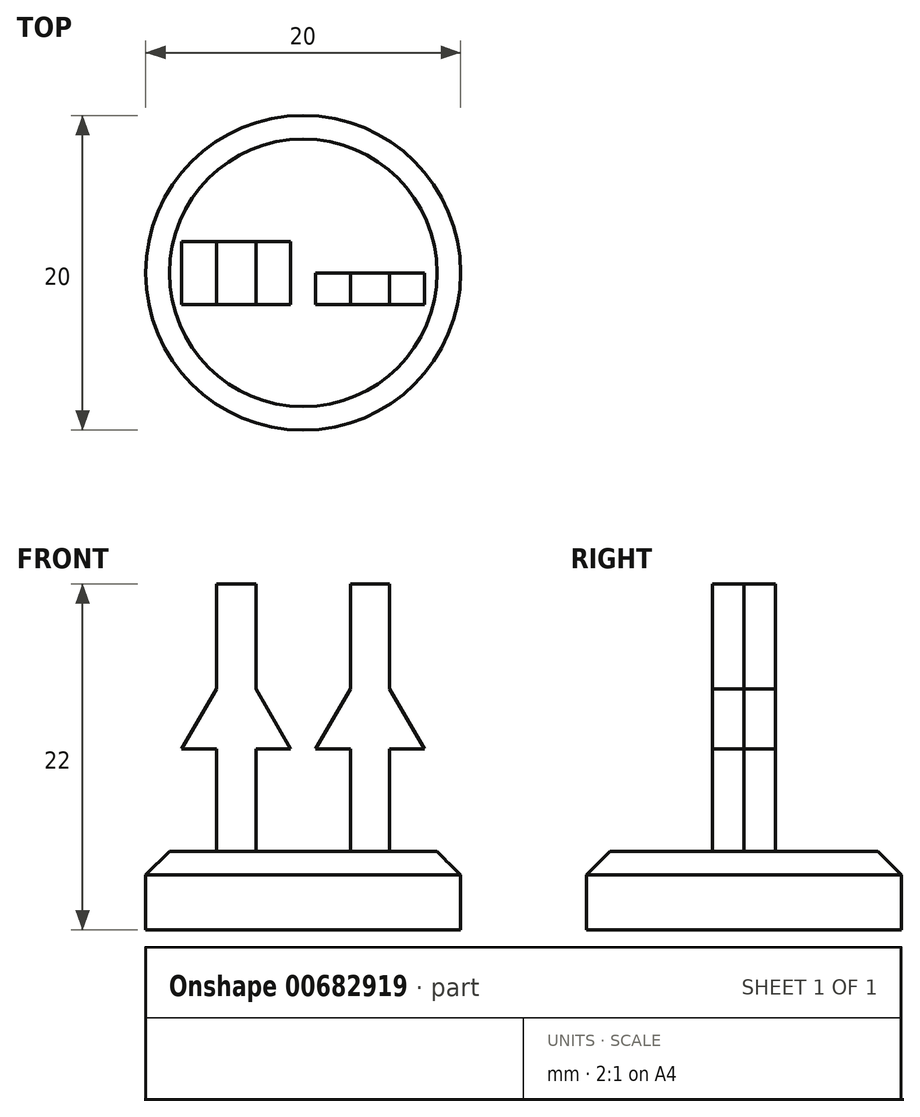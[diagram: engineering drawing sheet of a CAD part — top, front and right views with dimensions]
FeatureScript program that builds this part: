
annotation { "Feature Type Name" : "Feature", "Feature Type Description" : "" }
export const myFeature = defineFeature(function(context is Context, id is Id, definition is map)
    precondition{}
    {
        {
            var Q0;
            Q0=qCreatedBy(makeId("Top.planeOp"),FACE);
            var sketch = newSketch(context, id + "F0", { "sketchPlane" : qUnion([Q0])});
            skCircle(sketch, "E0", {"center": v(0, 0) * mm, "radius": 10 * mm});
            skSolve(sketch);
        }
        {
            var Q0;
            Q0=makeQuery(id+"F0.imprint","IMPRINT",FACE,{"disambiguationData":[TD([[makeQuery(id+"F0.imprint","IMPRINT",EDGE,{"derivedFrom":sQuery(id+"F0.wireOp",EDGE,"E0")}),1.0]])]});
            extrude(context, id + "F1", {"entities" : qUnion([Q0]), "depth" : 5 * mm, "offsetDistance" : 25 * mm});
        }
        {
            var Q0;
            Q0=makeQuery(id+"F1.opExtrude","CAP_EDGE",EDGE,{"disambiguationData":[OSD([sQuery(id+"F0.wireOp",EDGE,"E0")])],"isStart":false});
            chamfer(context, id + "F2", {"entities" : qUnion([Q0]), "width" : 1.5 * mm, "tangentPropagation" : true});
        }
        {
            var Q0;
            Q0=qCreatedBy(makeId("Front.planeOp"),FACE);
            var sketch = newSketch(context, id + "F3", { "sketchPlane" : qUnion([Q0])});
            skLineSegment(sketch, "E1", {"start": v(5.5, 13.5) * mm, "end": v(5.5, 5) * mm});
            skLineSegment(sketch, "E2", {"start": v(5.5, 13.5) * mm, "end": v(5.5, 22) * mm});
            skLineSegment(sketch, "E3", {"start": v(5.5, 22) * mm, "end": v(3, 22) * mm});
            skLineSegment(sketch, "E4", {"start": v(3, 22) * mm, "end": v(3, 5) * mm});
            skLineSegment(sketch, "E5", {"start": v(3, 5) * mm, "end": v(5.5, 5) * mm});
            skLineSegment(sketch, "E6", {"start": v(5.5, 13.5) * mm, "end": v(3, 13.5) * mm});
            skCircle(sketch, "E7.cCircle", {"center": v(4.25, 13.5) * mm, "radius": 2 * mm, "construction": true});
            skLineSegment(sketch, "E7.0", {"start": v(0.79, 11.5) * mm, "end": v(4.25, 17.5) * mm});
            skLineSegment(sketch, "E7.1", {"start": v(4.25, 17.5) * mm, "end": v(7.71, 11.5) * mm});
            skLineSegment(sketch, "E7.2", {"start": v(7.71, 11.5) * mm, "end": v(0.79, 11.5) * mm});
            skPoint(sketch, "E7.0.midPoint", {"position": v(2.52, 14.5) * mm});
            skLineSegment(sketch, "E8", {"start": v(5.5, 13.5) * mm, "end": v(5.5, 8.5) * mm});
            skLineSegment(sketch, "E9", {"start": v(5.5, 8.5) * mm, "end": v(5.5, 8) * mm});
            skLineSegment(sketch, "E10", {"start": v(5.5, 8.5) * mm, "end": v(5.5, 9) * mm});
            skLineSegment(sketch, "E11", {"start": v(-5.5, 9) * mm, "end": v(-5.5, 8) * mm});
            skLineSegment(sketch, "E12", {"start": v(5.5, 13.5) * mm, "end": v(5.5, 18.5) * mm});
            skLineSegment(sketch, "E13", {"start": v(5.5, 18.5) * mm, "end": v(5.5, 19) * mm});
            skLineSegment(sketch, "E14", {"start": v(-3.5, 19) * mm, "end": v(-3.5, 18) * mm});
            skLineSegment(sketch, "E15", {"start": v(-5.5, 8) * mm, "end": v(-5.5, 5) * mm});
            skLineSegment(sketch, "E16", {"start": v(-5.5, 5) * mm, "end": v(-3, 5) * mm});
            skLineSegment(sketch, "E17", {"start": v(-3, 5) * mm, "end": v(-3, 22) * mm});
            skLineSegment(sketch, "E18", {"start": v(-3, 22) * mm, "end": v(-5.5, 22) * mm});
            skLineSegment(sketch, "E19", {"start": v(-5.5, 22) * mm, "end": v(-5.5, 9) * mm});
            skLineSegment(sketch, "E20", {"start": v(-3, 13.5) * mm, "end": v(-5.5, 13.5) * mm});
            skCircle(sketch, "E21.cCircle", {"center": v(-4.25, 13.5) * mm, "radius": 2 * mm, "construction": true});
            skLineSegment(sketch, "E21.0", {"start": v(-7.71, 11.5) * mm, "end": v(-4.25, 17.5) * mm});
            skLineSegment(sketch, "E21.1", {"start": v(-4.25, 17.5) * mm, "end": v(-0.79, 11.5) * mm});
            skLineSegment(sketch, "E21.2", {"start": v(-0.79, 11.5) * mm, "end": v(-7.71, 11.5) * mm});
            skPoint(sketch, "E21.0.midPoint", {"position": v(-5.98, 14.5) * mm});
            skSolve(sketch);
        }
        {
            var Q0;
            {var subQ0=sQuery(id+"F3.wireOp",EDGE,"E15");Q0=makeQuery(id+"F3.imprint","IMPRINT",FACE,{"disambiguationData":[TD([[makeQuery(id+"F3.imprint","IMPRINT",EDGE,{"derivedFrom":subQ0}),1.0]])]});}
            var Q1;
            {var subQ0=sQuery(id+"F3.wireOp",EDGE,"E11");Q1=makeQuery(id+"F3.imprint","IMPRINT",FACE,{"disambiguationData":[TD([[makeQuery(id+"F3.imprint","IMPRINT",EDGE,{"derivedFrom":subQ0}),1.0]])]});}
            var Q2;
            {var subQ1=sQuery(id+"F3.wireOp",EDGE,"EQHTsxDi-yBak-7mSX-J8Yb-3IxzzojTnzbz");var subQ3=sQuery(id+"F3.wireOp",EDGE,"E17");var subQ4=makeQuery(id+"F3.imprint","INTERSECT",VERTEX,{"derivedFrom":[subQ1,subQ3]});Q2=makeQuery(id+"F3.imprint","IMPRINT",FACE,{"disambiguationData":[TD([[makeQuery(id+"F3.imprint","IMPRINT",EDGE,{"disambiguationData":[TD([[subQ4,-1.0]])],"derivedFrom":subQ3}),1.0]])]});}
            var Q3;
            {var subQ0=sQuery(id+"F3.wireOp",EDGE,"E17");var subQ1=makeQuery(id+"F3.imprint","INTERSECT",VERTEX,{"derivedFrom":[subQ0,sQuery(id+"F3.wireOp",EDGE,"E20")]});Q3=makeQuery(id+"F3.imprint","IMPRINT",FACE,{"disambiguationData":[TD([[makeQuery(id+"F3.imprint","IMPRINT",EDGE,{"disambiguationData":[TD([[subQ1,1.0]])],"derivedFrom":subQ0}),-1.0]])]});}
            var Q4;
            {var subQ0=sQuery(id+"F3.wireOp",EDGE,"E20");Q4=makeQuery(id+"F3.imprint","IMPRINT",FACE,{"disambiguationData":[TD([[makeQuery(id+"F3.imprint","IMPRINT",EDGE,{"derivedFrom":subQ0}),1.0]])]});}
            var Q5;
            {var subQ0=sQuery(id+"F3.wireOp",EDGE,"E20");Q5=makeQuery(id+"F3.imprint","IMPRINT",FACE,{"disambiguationData":[TD([[makeQuery(id+"F3.imprint","IMPRINT",EDGE,{"derivedFrom":subQ0}),-1.0]])]});}
            var Q6;
            {var subQ0=sQuery(id+"F3.wireOp",EDGE,"E19");var subQ1=makeQuery(id+"F3.imprint","INTERSECT",VERTEX,{"derivedFrom":[subQ0,sQuery(id+"F3.wireOp",EDGE,"E20")]});Q6=makeQuery(id+"F3.imprint","IMPRINT",FACE,{"disambiguationData":[TD([[makeQuery(id+"F3.imprint","IMPRINT",EDGE,{"disambiguationData":[TD([[subQ1,1.0]])],"derivedFrom":subQ0}),-1.0]])]});}
            var Q7;
            {var subQ3=sQuery(id+"F3.wireOp",EDGE,"E19");var subQ5=sQuery(id+"F3.wireOp",EDGE,"8I4BeRHs-Gmml-n6d2-LC97-bdPFLSqAeQXX");var subQ6=makeQuery(id+"F3.imprint","INTERSECT",VERTEX,{"derivedFrom":[subQ5,subQ3]});Q7=makeQuery(id+"F3.imprint","IMPRINT",FACE,{"disambiguationData":[TD([[makeQuery(id+"F3.imprint","IMPRINT",EDGE,{"disambiguationData":[TD([[subQ6,-1.0]])],"derivedFrom":subQ5}),-1.0]])]});}
            var Q8;
            {var subQ0=sQuery(id+"F3.wireOp",EDGE,"E19");var subQ1=sQuery(id+"F3.wireOp",EDGE,"mUdp0F8c-JpfW-iBtl-aqys-KmnHf74pH5AF");var subQ2=makeQuery(id+"F3.imprint","INTERSECT",VERTEX,{"derivedFrom":[subQ1,subQ0]});Q8=makeQuery(id+"F3.imprint","IMPRINT",FACE,{"disambiguationData":[TD([[makeQuery(id+"F3.imprint","IMPRINT",EDGE,{"disambiguationData":[TD([[subQ2,1.0]])],"derivedFrom":subQ1}),1.0]])]});}
            var Q9;
            {var subQ5=sQuery(id+"F3.wireOp",EDGE,"E18");Q9=makeQuery(id+"F3.imprint","IMPRINT",FACE,{"disambiguationData":[TD([[makeQuery(id+"F3.imprint","IMPRINT",EDGE,{"derivedFrom":subQ5}),1.0]])]});}
            var Q10;
            {var subQ0=sQuery(id+"F3.wireOp",EDGE,"E2");Q10=makeQuery(id+"F3.imprint","IMPRINT",FACE,{"disambiguationData":[TD([[makeQuery(id+"F3.imprint","IMPRINT",EDGE,{"derivedFrom":subQ0}),1.0]])]});}
            var Q11;
            {var subQ1=sQuery(id+"F3.wireOp",EDGE,"E13");Q11=makeQuery(id+"F3.imprint","IMPRINT",FACE,{"disambiguationData":[TD([[makeQuery(id+"F3.imprint","IMPRINT",EDGE,{"derivedFrom":subQ1}),1.0]])]});}
            var Q12;
            {var subQ0=sQuery(id+"F3.wireOp",EDGE,"mUdp0F8c-JpfW-iBtl-aqys-KmnHf74pH5AF");var subQ1=sQuery(id+"F3.wireOp",EDGE,"E4");var subQ2=makeQuery(id+"F3.imprint","INTERSECT",VERTEX,{"derivedFrom":[subQ1,subQ0]});Q12=makeQuery(id+"F3.imprint","IMPRINT",FACE,{"disambiguationData":[TD([[makeQuery(id+"F3.imprint","IMPRINT",EDGE,{"disambiguationData":[TD([[subQ2,-1.0]])],"derivedFrom":subQ1}),-1.0]])]});}
            var Q13;
            {var subQ0=sQuery(id+"F3.wireOp",EDGE,"8I4BeRHs-Gmml-n6d2-LC97-bdPFLSqAeQXX");var subQ7=sQuery(id+"F3.wireOp",EDGE,"E4");var subQ9=makeQuery(id+"F3.imprint","INTERSECT",VERTEX,{"derivedFrom":[subQ7,subQ0]});Q13=makeQuery(id+"F3.imprint","IMPRINT",FACE,{"disambiguationData":[TD([[makeQuery(id+"F3.imprint","IMPRINT",EDGE,{"disambiguationData":[TD([[subQ9,-1.0]])],"derivedFrom":subQ7}),1.0]])]});}
            var Q14;
            {var subQ7=sQuery(id+"F3.wireOp",EDGE,"E6");Q14=makeQuery(id+"F3.imprint","IMPRINT",FACE,{"disambiguationData":[TD([[makeQuery(id+"F3.imprint","IMPRINT",EDGE,{"derivedFrom":subQ7}),-1.0]])]});}
            var Q15;
            {var subQ0=sQuery(id+"F3.wireOp",EDGE,"E4");var subQ1=makeQuery(id+"F3.imprint","INTERSECT",VERTEX,{"derivedFrom":[subQ0,sQuery(id+"F3.wireOp",EDGE,"E6")]});Q15=makeQuery(id+"F3.imprint","IMPRINT",FACE,{"disambiguationData":[TD([[makeQuery(id+"F3.imprint","IMPRINT",EDGE,{"disambiguationData":[TD([[subQ1,1.0]])],"derivedFrom":subQ0}),-1.0]])]});}
            var Q16;
            {var subQ0=sQuery(id+"F3.wireOp",EDGE,"E6");Q16=makeQuery(id+"F3.imprint","IMPRINT",FACE,{"disambiguationData":[TD([[makeQuery(id+"F3.imprint","IMPRINT",EDGE,{"derivedFrom":subQ0}),1.0]])]});}
            var Q17;
            {var subQ3=sQuery(id+"F3.wireOp",EDGE,"E7.1");var subQ5=sQuery(id+"F3.wireOp",EDGE,"E7.2");var subQ6=makeQuery(id+"F3.imprint","INTERSECT",VERTEX,{"derivedFrom":[subQ3,subQ5]});Q17=makeQuery(id+"F3.imprint","IMPRINT",FACE,{"disambiguationData":[TD([[makeQuery(id+"F3.imprint","IMPRINT",EDGE,{"disambiguationData":[TD([[subQ6,1.0]])],"derivedFrom":subQ3}),-1.0]])]});}
            var Q18;
            {var subQ1=sQuery(id+"F3.wireOp",EDGE,"Y9C8eTe3-88fX-KXNt-j7JQ-pDCD70UgcZAf");var subQ3=sQuery(id+"F3.wireOp",EDGE,"E7.1");var subQ4=makeQuery(id+"F3.imprint","INTERSECT",VERTEX,{"derivedFrom":[subQ1,subQ3]});Q18=makeQuery(id+"F3.imprint","IMPRINT",FACE,{"disambiguationData":[TD([[makeQuery(id+"F3.imprint","IMPRINT",EDGE,{"disambiguationData":[TD([[subQ4,1.0]])],"derivedFrom":subQ3}),-1.0]])]});}
            var Q19;
            {var subQ0=sQuery(id+"F3.wireOp",EDGE,"E7.2");var subQ1=sQuery(id+"F3.wireOp",EDGE,"E4");var subQ2=makeQuery(id+"F3.imprint","INTERSECT",VERTEX,{"derivedFrom":[subQ1,subQ0]});Q19=makeQuery(id+"F3.imprint","IMPRINT",FACE,{"disambiguationData":[TD([[makeQuery(id+"F3.imprint","IMPRINT",EDGE,{"disambiguationData":[TD([[subQ2,-1.0]])],"derivedFrom":subQ1}),1.0]])]});}
            var Q20;
            {var subQ1=sQuery(id+"F3.wireOp",EDGE,"E9");Q20=makeQuery(id+"F3.imprint","IMPRINT",FACE,{"disambiguationData":[TD([[makeQuery(id+"F3.imprint","IMPRINT",EDGE,{"derivedFrom":subQ1}),-1.0]])]});}
            var Q21;
            {var subQ0=sQuery(id+"F3.wireOp",EDGE,"E1");Q21=makeQuery(id+"F3.imprint","IMPRINT",FACE,{"disambiguationData":[TD([[makeQuery(id+"F3.imprint","IMPRINT",EDGE,{"derivedFrom":subQ0}),-1.0]])]});}
            var Q22;
            {var subQ0=sQuery(id+"F3.wireOp",EDGE,"Q0sZmuIG-eceH-zXUB-db0S-FeUkpUr2JhbU");var subQ1=sQuery(id+"F3.wireOp",EDGE,"E4");var subQ2=makeQuery(id+"F3.imprint","INTERSECT",VERTEX,{"derivedFrom":[subQ1,subQ0]});Q22=makeQuery(id+"F3.imprint","IMPRINT",FACE,{"disambiguationData":[TD([[makeQuery(id+"F3.imprint","IMPRINT",EDGE,{"disambiguationData":[TD([[subQ2,1.0]])],"derivedFrom":subQ1}),-1.0]])]});}
            extrude(context, id + "F4", {"entities" : qUnion([Q0, Q1, Q2, Q3, Q4, Q5, Q6, Q7, Q8, Q9, Q10, Q11, Q12, Q13, Q14, Q15, Q16, Q17, Q18, Q19, Q20, Q21, Q22]), "operationType" : NewBodyOperationType.ADD, "depth" : 2 * mm, "offsetDistance" : 25 * mm});
        }
        {
            var Q0;
            Q0=makeQuery(id+"F4.opExtrude","CAP_FACE",FACE,{"disambiguationData":[OSD([sQuery(id+"F3.wireOp",EDGE,"E1"),sQuery(id+"F3.wireOp",EDGE,"E2"),sQuery(id+"F3.wireOp",EDGE,"E3"),sQuery(id+"F3.wireOp",EDGE,"E4"),sQuery(id+"F3.wireOp",EDGE,"E5"),sQuery(id+"F3.wireOp",EDGE,"E7.0"),sQuery(id+"F3.wireOp",EDGE,"E7.1"),sQuery(id+"F3.wireOp",EDGE,"E7.2"),sQuery(id+"F3.wireOp",EDGE,"E8"),sQuery(id+"F3.wireOp",EDGE,"E9"),sQuery(id+"F3.wireOp",EDGE,"Q0sZmuIG-eceH-zXUB-db0S-FeUkpUr2JhbU"),sQuery(id+"F3.wireOp",EDGE,"E10"),sQuery(id+"F3.wireOp",EDGE,"EQHTsxDi-yBak-7mSX-J8Yb-3IxzzojTnzbz"),sQuery(id+"F3.wireOp",EDGE,"E11"),sQuery(id+"F3.wireOp",EDGE,"E12"),sQuery(id+"F3.wireOp",EDGE,"E13"),sQuery(id+"F3.wireOp",EDGE,"mUdp0F8c-JpfW-iBtl-aqys-KmnHf74pH5AF"),sQuery(id+"F3.wireOp",EDGE,"8I4BeRHs-Gmml-n6d2-LC97-bdPFLSqAeQXX"),sQuery(id+"F3.wireOp",EDGE,"E15"),sQuery(id+"F3.wireOp",EDGE,"E16"),sQuery(id+"F3.wireOp",EDGE,"E17"),sQuery(id+"F3.wireOp",EDGE,"E18"),sQuery(id+"F3.wireOp",EDGE,"E19"),sQuery(id+"F3.wireOp",EDGE,"E21.0"),sQuery(id+"F3.wireOp",EDGE,"E21.1"),sQuery(id+"F3.wireOp",EDGE,"E21.2")])],"isStart":true});
            var Q1;
            Q1=makeQuery(id+"F4.opExtrude","CAP_FACE",FACE,{"disambiguationData":[OSD([sQuery(id+"F3.wireOp",EDGE,"E11"),sQuery(id+"F3.wireOp",EDGE,"E15"),sQuery(id+"F3.wireOp",EDGE,"E16"),sQuery(id+"F3.wireOp",EDGE,"E17"),sQuery(id+"F3.wireOp",EDGE,"E18"),sQuery(id+"F3.wireOp",EDGE,"E19"),sQuery(id+"F3.wireOp",EDGE,"E21.0"),sQuery(id+"F3.wireOp",EDGE,"E21.1"),sQuery(id+"F3.wireOp",EDGE,"E21.2")])],"isStart":true});
            extrude(context, id + "F5", {"entities" : qUnion([Q0, Q1]), "operationType" : NewBodyOperationType.ADD, "depth" : 2 * mm, "offsetDistance" : 25 * mm});
        }
    });
